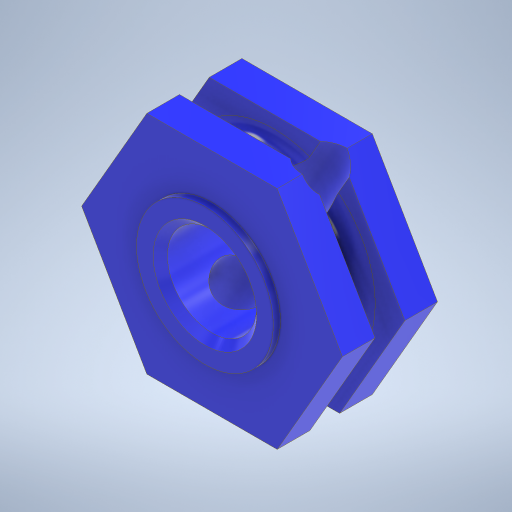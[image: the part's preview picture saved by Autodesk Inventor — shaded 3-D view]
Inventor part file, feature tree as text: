
AUTODESK INVENTOR PART (.ipt)
format: ipt  version: 2024 (Build 280153000, 153)  size: 363,520 bytes
history: native  units: in
note: dims shown in document units (in); Inventor stores cm internally (conversion verified against a paired STEP export)
features: extrude x4, sketch x4, plane x2, chamfer x1, revolve x1, direct_edit x1, other x1
ambient origin geometry x8: Origin, YZ Plane, XZ Plane, XY Plane, X Axis, Y Axis, Z Axis, Center Point
bodies: Solid1 (feature_tree)
feature tree (14):
  extrude  "Extrusion1"  Depth=0.2in TaperAngle=0.0deg
  sketch  "Sketch2"  dims[d3=0.1875in d4=0.05in]
  extrude  "Extrusion2"  Depth=0.05in
  extrude  "Extrusion3"  Depth=0.015in TaperAngle=0.0deg
  chamfer  "Chamfer1"  Distance=0.015in Angle=45.0deg
  plane  "Work Plane1"
  extrude  "Extrusion4"  Depth=3.937in
  plane  "Work Plane3"
  revolve  "Revolution1"  [1 undecoded]
  direct_edit  "Direct Edit1"
  sketch  "Sketch1"  dims[d0=0.475in d1=0.2in d2=0.0in]
  sketch  "Sketch3"  dims[d5=0.2in d6=0.0in d7=0.015in d8=0.0in d9=0.015in d10=0.125in d11=45.0deg]
  sketch  "Sketch7"  dims[d12=90.0deg d13=0.0938in d14=0.015in d15=0.0in d16=0.0625in d17=0.0625in d18=90.0deg d19=3.937in d20=0.3937in d21=0.3937in]
  other  "Scale1"
note: 1 required parameter value undecoded (feature->parameter linkage not recoverable at this tier; creation-order binding heuristic only, values carry confidence <= 0.55)
